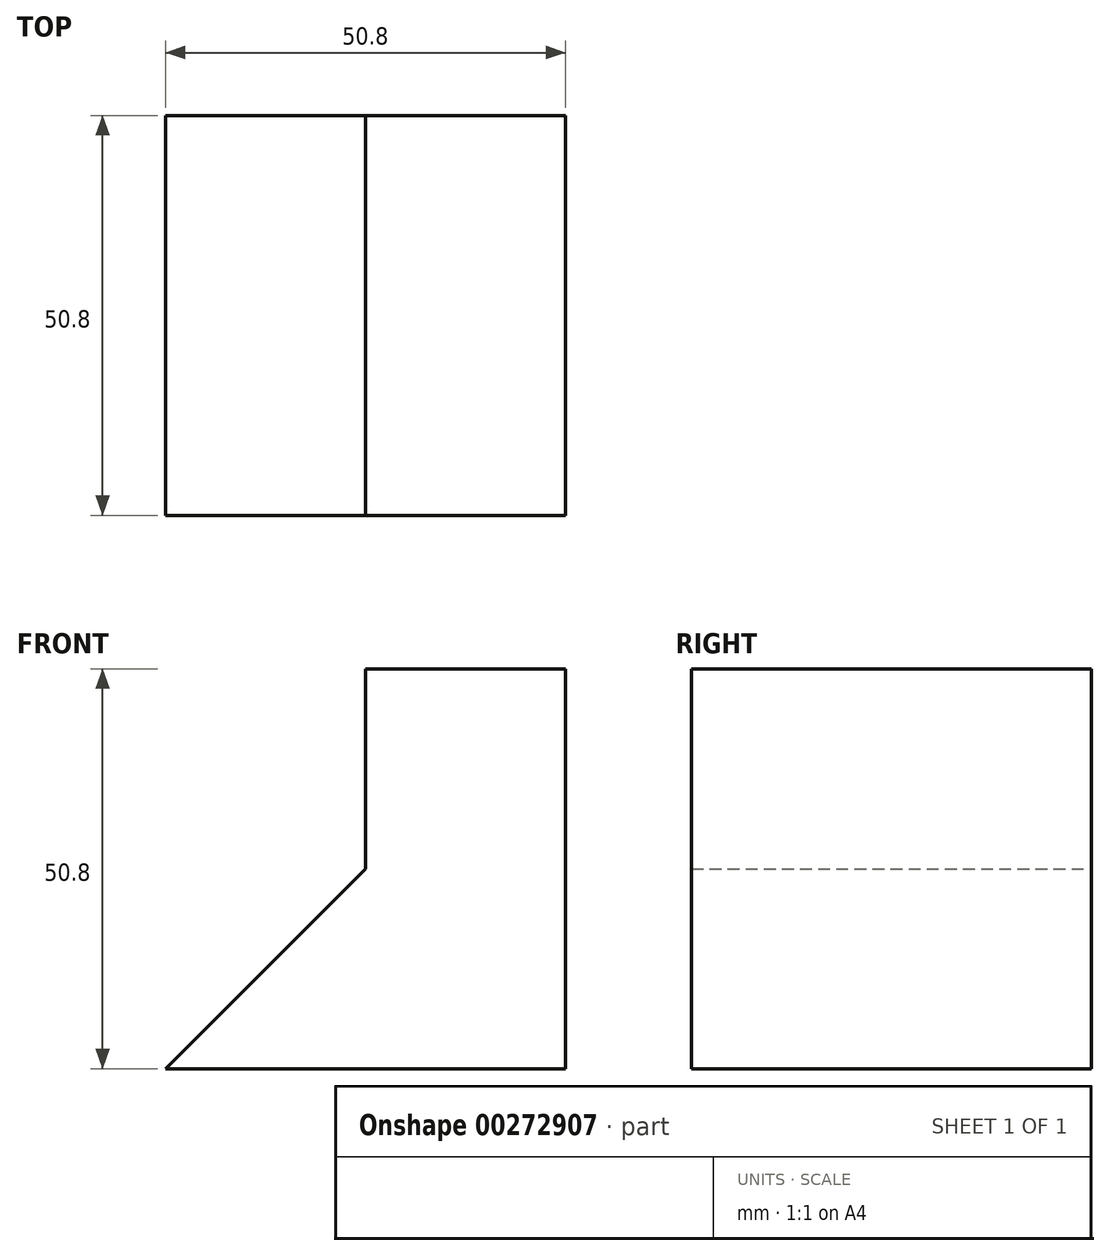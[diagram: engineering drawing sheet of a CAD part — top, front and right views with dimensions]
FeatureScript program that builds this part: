
annotation { "Feature Type Name" : "Feature", "Feature Type Description" : "" }
export const myFeature = defineFeature(function(context is Context, id is Id, definition is map)
    precondition{}
    {
        {
            var Q0;
            Q0=qCreatedBy(makeId("Front.planeOp"),FACE);
            var sketch = newSketch(context, id + "F0", { "sketchPlane" : qUnion([Q0])});
            skLineSegment(sketch, "E0", {"start": v(0, 0) * mm, "end": v(0, 50.8) * mm});
            skLineSegment(sketch, "E1", {"start": v(0, 50.8) * mm, "end": v(-25.4, 50.8) * mm});
            skLineSegment(sketch, "E2", {"start": v(-25.4, 50.8) * mm, "end": v(-25.4, 25.4) * mm});
            skLineSegment(sketch, "E3", {"start": v(0, 0) * mm, "end": v(-50.8, 0) * mm});
            skLineSegment(sketch, "E4", {"start": v(-50.8, 0) * mm, "end": v(-25.4, 25.4) * mm});
            skSolve(sketch);
        }
        {
            var Q0;
            Q0 = qSketchRegion(id + "F0", true);
            extrude(context, id + "F1", {"entities" : qUnion([Q0]), "depth" : 50.8 * mm});
        }
    });
